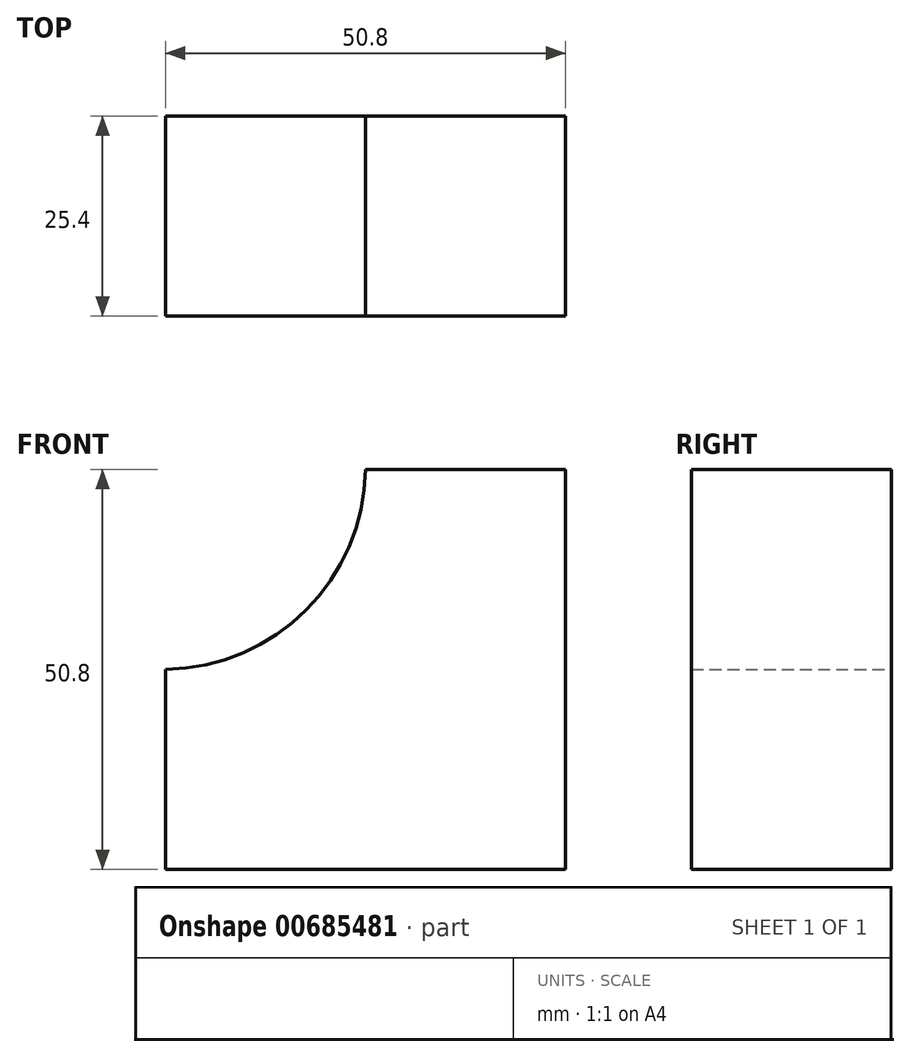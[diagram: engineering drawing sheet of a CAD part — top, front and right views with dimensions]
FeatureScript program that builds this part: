
annotation { "Feature Type Name" : "Feature", "Feature Type Description" : "" }
export const myFeature = defineFeature(function(context is Context, id is Id, definition is map)
    precondition{}
    {
        {
            var Q0;
            Q0=qCreatedBy(makeId("Front.planeOp"),FACE);
            var sketch = newSketch(context, id + "F0", { "sketchPlane" : qUnion([Q0])});
            skLineSegment(sketch, "E0", {"start": v(-25.4, 50.8) * mm, "end": v(0, 50.8) * mm});
            skLineSegment(sketch, "E1", {"start": v(0, 50.8) * mm, "end": v(0, 0) * mm});
            skLineSegment(sketch, "E2", {"start": v(0, 0) * mm, "end": v(-50.8, 0) * mm});
            skLineSegment(sketch, "E3", {"start": v(-50.8, 0) * mm, "end": v(-50.8, 25.4) * mm});
            skArc(sketch, "E4", {"start": v(-50.8, 25.4) * mm, "mid": v(-32.95, 32.95) * mm, "end": v(-25.4, 50.8) * mm});
            skSolve(sketch);
        }
        {
            var Q0;
            Q0 = qSketchRegion(id + "F0", true);
            extrude(context, id + "F1", {"entities" : qUnion([Q0]), "depth" : 25.4 * mm, "offsetDistance" : 25.4 * mm});
        }
    });
